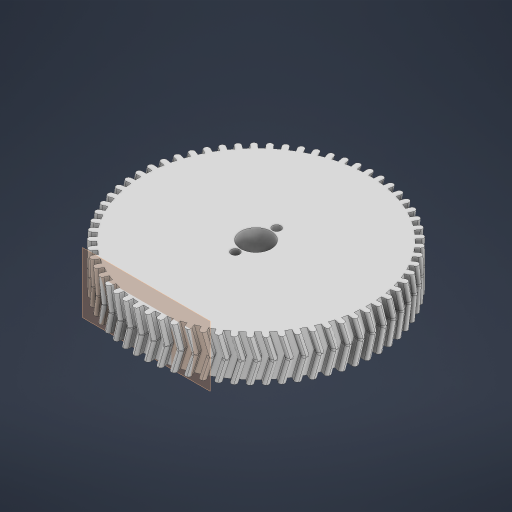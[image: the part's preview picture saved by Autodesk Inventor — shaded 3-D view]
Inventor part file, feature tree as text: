
AUTODESK INVENTOR PART (.ipt)
format: ipt  version: 2023 (Build 270158030, 158C)  size: 1,182,208 bytes
history: native  units: in
note: dims shown in document units (in); Inventor stores cm internally (conversion verified against a paired STEP export)
features: extrude x6, sketch x6, plane x1, fillet x1, pattern_circular x1
ambient origin geometry x8: Origin, YZ Plane, XZ Plane, XY Plane, X Axis, Y Axis, Z Axis, Center Point
bodies: Solid1 (feature_tree)
feature tree (15):
  extrude  "Extrusion1"  Depth=0.5906in TaperAngle=0.0deg
  plane  "Work Plane1"
  extrude  "Extrusion2"  Depth=1.565in
  extrude  "Extrusion3"  Depth=0.0787in
  fillet  "Fillet2"  Radius=0.1378in
  pattern_circular  "Circular Pattern3"  Count=6  [1 undecoded]
  extrude  "Extrusion6"  Depth=0.5512in TaperAngle=360.0deg
  extrude  "Extrusion7"  Depth=0.5512in
  extrude  "Extrusion8"  Depth=0.0394in TaperAngle=0.0deg
  sketch  "Sketch3"  dims[d0=3.2087in d1=0.5906in d2=0.0in]
  sketch  "Sketch8"  dims[d3=1.565in d4=0.0787in]
  sketch  "Sketch10"  dims[d5=0.0787in d6=0.0787in d7=0.1378in d8=0.0in]
  sketch  "Sketch18"  dims[d17=0.1969in]
  sketch  "Sketch20"  dims[d18=0.1732in d19=2.3622in d20=0.0in]
  sketch  "Sketch21"  dims[d25=0.0394in d26=25.5906in d27=360.0deg d36=0.874in d37=0.0394in d38=0.0in d39=0.4331in d40=0.5512in d41=0.0in d42=0.1181in d43=0.1181in d44=0.5906in d45=0.2953in d46=0.5512in d47=0.0in]
note: 1 required parameter value undecoded (feature->parameter linkage not recoverable at this tier; creation-order binding heuristic only, values carry confidence <= 0.55)
